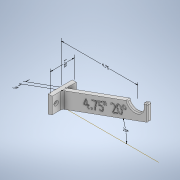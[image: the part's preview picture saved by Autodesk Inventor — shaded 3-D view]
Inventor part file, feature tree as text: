
AUTODESK INVENTOR PART (.ipt)
format: ipt  version: 2021.1 (Build 251245010, 245A)  size: 515,584 bytes
history: native  units: in
note: dims shown in document units (in); Inventor stores cm internally (conversion verified against a paired STEP export)
features: sketch x6, other x5, extrude x5, fillet x4, hole x1
ambient origin geometry x8: Origin, YZ Plane, XZ Plane, XY Plane, X Axis, Y Axis, Z Axis, Center Point
bodies: Solid2 (feature_tree)
feature tree (21):
  other  "Annotations"
  extrude  "Extrusion3"  Depth=0.25in
  extrude  "Extrusion4"  Depth=0.1374in
  sketch  "Sketch7"  dims[d26=1.075in d29=0.25in]
  extrude  "Extrusion5"  Depth=0.25in
  hole  "Hole3"  [1 undecoded]
  fillet  "Fillet3"  [1 undecoded]
  fillet  "Fillet4"  [1 undecoded]
  fillet  "Fillet5"  Radius=0.25in
  fillet  "Fillet6"  Radius=0.25in
  extrude  "Extrusion6"  Depth=0.0625in
  extrude  "Extrusion7"  Depth=0.0625in
  sketch  "Sketch5"  dims[d21=1.0in d22=0.25in]
  sketch  "Sketch6"  dims[d23=1.5in d24=0.0in d25=0.1374in]
  sketch  "Sketch8"  dims[d30=4.75in d31=0.25in d32=0.0in d33=0.0in d34=0.25in d35=0.25in]
  sketch  "Sketch9"  dims[d47=1.5in d48=0.0in]
  sketch  "Sketch10"  dims[d49=0.15in d50=0.75in d51=0.279in d52=0.25in d53=0.5635in d54=1.0in d55=0.8108in d65=0.0625in d66=0.0625in d67=0.0625in d68=0.125in d72=0.05in d73=0.0in d74=0.05in d75=0.0in d56=0.2085in d57=0.331in d58=1.5in d59=2.3174in d60=0.1374in d69=4.75in d70=0.3005in d71=0.25in]
  other  "Linear Dimension 1"
  other  "Angular Dimension 1"
  other  "Linear Dimension 2"
  other  "Linear Dimension 3"
note: 3 required parameter values undecoded (feature->parameter linkage not recoverable at this tier; creation-order binding heuristic only, values carry confidence <= 0.55)
